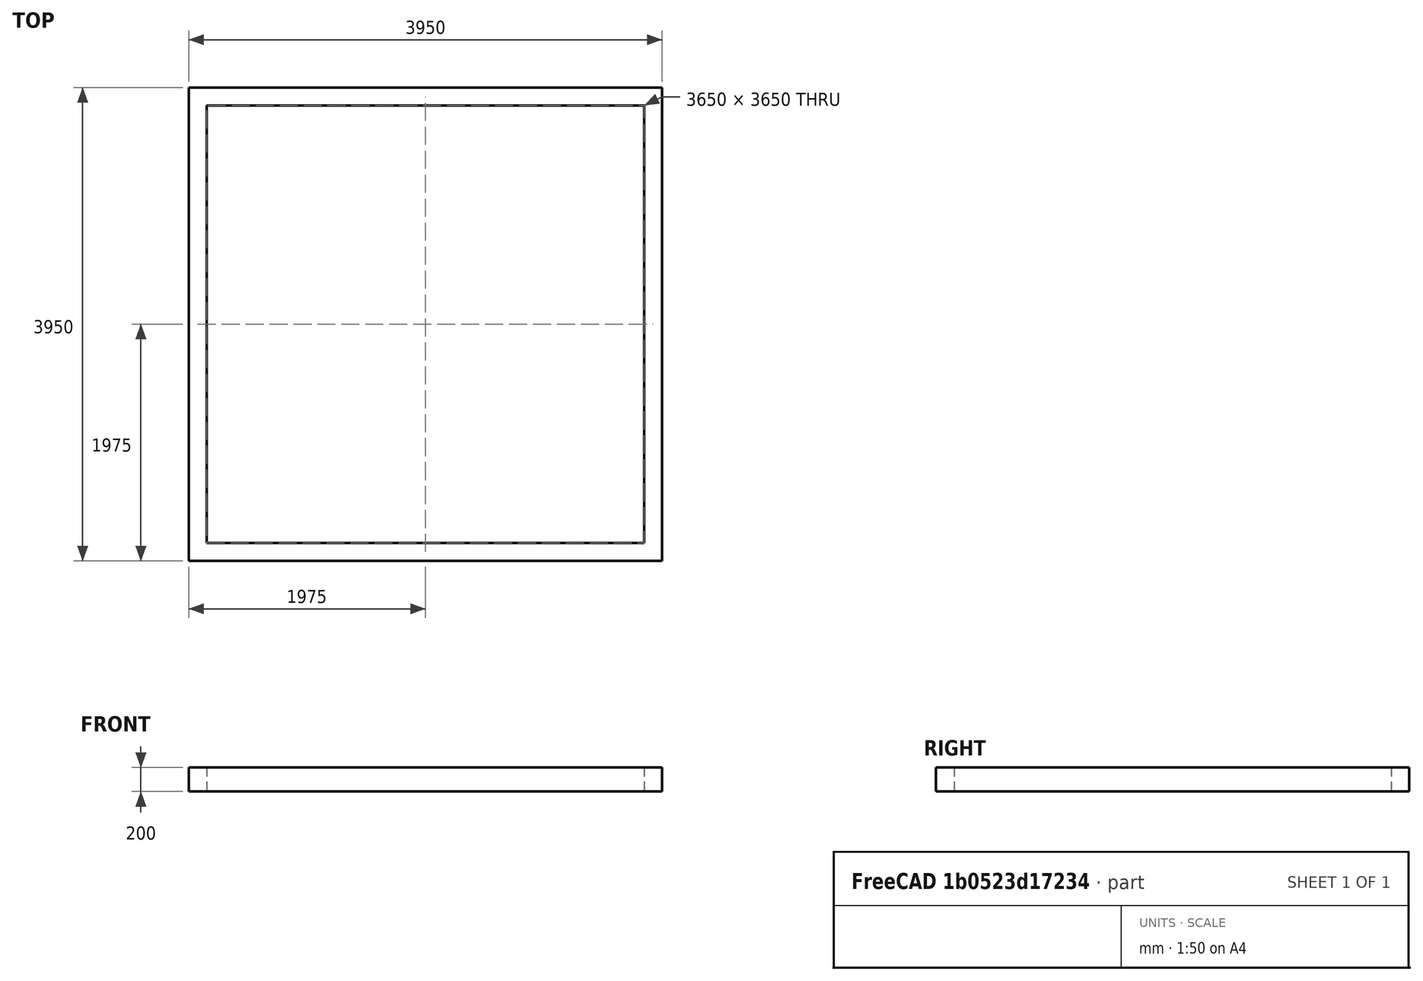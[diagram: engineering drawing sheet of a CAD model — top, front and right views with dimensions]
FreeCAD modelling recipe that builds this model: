
FCSTD DOCUMENT  (FreeCAD 0.20R29177 +426 (Git))
Label: ASM_Main
License: All rights reserved
LicenseURL: http://en.wikipedia.org/wiki/All_rights_reserved
objects: App::Link×4, App::DocumentObjectGroup×3, PartDesign::CoordinateSystem×1, App::FeaturePython×1, Part::FeaturePython×1, Sketcher::SketchObject×1, PartDesign::Pad×1, PartDesign::Body×1, App::Part×1
note: 6 computed .brp shape members not serialized (recipe doc carries the construction recipe); baked Part::Feature solids carry a one-line shape summary decoded from their .brp
EXTERNAL_REF file=ASM_Base.FCStd obj=LCS_Origin
EXTERNAL_REF file=ASM_Base.FCStd obj=Assembly
EXTERNAL_REF file=ASM_Platform.FCStd obj=ComputerPlatform_LCS_TopPivot
EXTERNAL_REF file=PlayStation5.FCStd obj=LCS_Origin
EXTERNAL_REF file=PlayStation5.FCStd obj=Assembly
EXTERNAL_REF file=ASM_TurnTable.FCStd obj=LCS_Origin
EXTERNAL_REF file=ASM_TurnTable.FCStd obj=Assembly
EXTERNAL_REF file=ASM_Platform.FCStd obj=Assembly
EXTERNAL_REF file=ASM_Platform.FCStd obj=LCS_Origin
EXTERNAL_REF file=Params.FCStd obj=Spreadsheet
EXTERNAL_REF file=../../../../../../AppData/Local/Temp/FreeCAD/Cache/FreeCAD_Doc_690303f0-95d3-45ba-b895-2698c964fae2_da39a3_1928 obj=LCS_Origin
EXTERNAL_REF file=../../../../../../AppData/Local/Temp/FreeCAD/Cache/FreeCAD_Doc_690303f0-95d3-45ba-b895-2698c964fae2_da39a3_1928 obj=Assembly
EXTERNAL_REF file=ASM_ExtensionArm.FCStd obj=Assembly

FEATURE [App::DocumentObjectGroup] Parts
FEATURE [PartDesign::CoordinateSystem] LCS_Origin
  AttacherType = Attacher::AttachEngine3D
  MapMode = 2
  Support = -> [X_Axis]
FEATURE [App::FeaturePython] Variables  # WARN: FeaturePython — macro-defined, semantics opaque (R4)
  Retraction = 0
  Rotation = 0
  Type = App::PropertyContainer
FEATURE [App::DocumentObjectGroup] Constraints
FEATURE [App::DocumentObjectGroup] Configurations
FEATURE [App::Link] ASM_Base
  AttachedBy = #LCS_Origin
  AttachedTo = Parent Assembly#LCS_Origin
  LinkedObject = -> <external ASM_Base.FCStd>#Assembly
  SolverId = Asm4EE
  expr: Placement = LCS_Origin.Placement * AttachmentOffset * ASM_Base#LCS_Origin.Placement ^ -1
FEATURE [App::Link] PlayStation5
  AttachedBy = #LCS_Origin
  AttachedTo = ASM_Platform#ComputerPlatform_LCS_TopPivot
  AttachmentOffset = pos=(0,-220,0) rot=(0,0,1;1.5708rad)
  LinkPlacement = pos=(0,-220,-100) rot=(0,0,1;1.5708rad)
  LinkedObject = -> <external PlayStation5.FCStd>#Assembly
  Placement = pos=(0,-220,-100) rot=(0,0,1;1.5708rad)
  SolverId = Asm4EE
  expr: Placement = ASM_Platform.Placement * ASM_Platform#ComputerPlatform_LCS_TopPivot.Placement * AttachmentOffset * PlayStation5#LCS_Origin.Placement ^ -1
FEATURE [App::Link] ASM_TurnTable
  AttachedBy = #LCS_Origin
  AttachedTo = ASM_Base#LCS_Origin
  AttachmentOffset = pos=(0,0,-20) rot=(0,0,1;0rad)
  LinkPlacement = pos=(0,0,-20) rot=(0,0,1;0rad)
  LinkedObject = -> <external ASM_TurnTable.FCStd>#Assembly
  Placement = pos=(0,0,-20) rot=(0,0,1;0rad)
  SolverId = Asm4EE
  expr: .AttachmentOffset.Rotation.Angle = <<Variables>>.Rotation
  expr: Placement = ASM_Base.Placement * ASM_Base#LCS_Origin.Placement * AttachmentOffset * ASM_TurnTable#LCS_Origin.Placement ^ -1
FEATURE [App::Link] ASM_Platform
  AttachedBy = #ComputerPlatform_LCS_TopPivot
  AttachedTo = ASM_TurnTable#LCS_Origin
  AttachmentOffset = pos=(0,0,-80) rot=(0,0,1;0rad)
  LinkPlacement = pos=(0,0,-102.656) rot=(0,0,1;0rad)
  LinkedObject = -> <external ASM_Platform.FCStd>#Assembly
  Placement = pos=(0,0,-102.656) rot=(0,0,1;0rad)
  SolverId = Asm4EE
  expr: Placement = ASM_TurnTable.Placement * ASM_TurnTable#LCS_Origin.Placement * AttachmentOffset * ASM_Platform#ComputerPlatform_LCS_TopPivot.Placement ^ -1
FEATURE [Part::FeaturePython] ASM_ExtensionArm_var  # link proxy (typed FeaturePython)
  AttachedBy = #LCS_Origin
  AttachedTo = ASM_Platform#LCS_Origin
  AttachmentOffset = pos=(23,0,0) rot=(0,0,1;0rad)
  LinkedObject = -> <external ../../../../../../AppData/Local/Temp/FreeCAD/Cache/FreeCAD_Doc_690303f0-95d3-45ba-b895-2698c964fae2_da39a3_1928>#Assembly
  Placement = pos=(23,0,-102.656) rot=(0,0,1;0rad)
  Retraction = 0
  SolverId = Asm4EE
  SourceObject = -> <external ASM_ExtensionArm.FCStd>#Assembly
  expr: .AttachmentOffset.Base.x = <<Params>>#<<Params>>.ExtensionArmCenterOffset
  expr: Placement = ASM_Platform.Placement * ASM_Platform#LCS_Origin.Placement * AttachmentOffset * varTmpDoc_2#LCS_Origin.Placement ^ -1
  expr: Retraction = <<Variables>>.Retraction
FEATURE [Sketcher::SketchObject] Sketch
  FullyConstrained = true
  MapMode = 5
  Support = -> [XY_Plane001]
  expr: Constraints[10] = <<Params>>#<<Params>>.RoomLength
  expr: Constraints[9] = <<Params>>#<<Params>>.RoomWidth
  sketch-geometry (11):
    g0: LineSegment StartX=-1825 StartY=-1825 StartZ=0 EndX=-1825 EndY=1825 EndZ=0
    g1: LineSegment StartX=-1825 StartY=1825 StartZ=0 EndX=1825 EndY=1825 EndZ=0
    g2: LineSegment StartX=1825 StartY=1825 StartZ=0 EndX=1825 EndY=-1825 EndZ=0
    g3: LineSegment StartX=1825 StartY=-1825 StartZ=0 EndX=-1825 EndY=-1825 EndZ=0
    g4: GeomPoint X=0 Y=0 Z=0
    g5: LineSegment StartX=1975 StartY=1975 StartZ=0 EndX=1975 EndY=-1975 EndZ=0
    g6: LineSegment StartX=1975 StartY=-1975 StartZ=0 EndX=-1975 EndY=-1975 EndZ=0
    g7: LineSegment StartX=-1975 StartY=-1975 StartZ=0 EndX=-1975 EndY=1975 EndZ=0
    g8: LineSegment StartX=-1975 StartY=1975 StartZ=0 EndX=1975 EndY=1975 EndZ=0
    g9: GeomPoint X=0 Y=0 Z=0
    g10: LineSegment StartX=-1825 StartY=1825 StartZ=0 EndX=-1975 EndY=1975 EndZ=0
  constraints (26):
    c: Coincident(g0,g1)
    c: Coincident(g1,g2)
    c: Coincident(g2,g3)
    c: Coincident(g3,g0)
    c: Horizontal(g1)
    c: Horizontal(g3)
    c: Vertical(g0)
    c: Vertical(g2)
    c: Symmetric(g1,g0,g4)
    c: DistanceY(g2,g2) = 3650
    c: DistanceX(g3,g3) = 3650
    c: Coincident(g5,g6)
    c: Coincident(g6,g7)
    c: Coincident(g7,g8)
    c: Coincident(g8,g5)
    c: Horizontal(g6)
    c: Horizontal(g8)
    c: Vertical(g5)
    c: Vertical(g7)
    c: Symmetric(g6,g5,g9)
    c: Coincident(g9,g4)
    c: Coincident(g10,g0)
    c: Coincident(g10,g7)
    c: Angle(g10,g8) = 0.785398
    c: DistanceY(g0,g7) = 150
    c: Coincident(g4,g-1)
FEATURE [PartDesign::Pad] Pad
  Direction = (0,0,1)
  Length = 200
  Length2 = 10
  Profile = -> Sketch
  ReferenceAxis = -> Sketch [N_Axis]
  Reversed = true
  Type = 0
  expr: Length = 200
FEATURE [PartDesign::Body] Body  label="Room"
  Group = -> [Sketch,Pad]
  Origin = -> Origin001
  Tip = -> Pad
FEATURE [App::Part] Assembly
  AssemblyType = Part::Link
  Group = -> [LCS_Origin,Variables,Constraints,Configurations,ASM_Base,PlayStation5,ASM_TurnTable,ASM_Platform,ASM_ExtensionArm_var,Body]
  Origin = -> Origin
  Type = Assembly

RESOLVED EXTERNAL PARTS (link-assembly join: the EXTERNAL_REF files above that resolve inside this repo's crawl, each included once):
---- part ASM_Base.FCStd = doc fcstd_a2ac483629b0 ----
FCSTD DOCUMENT  (FreeCAD 0.20R29177 +426 (Git))
Label: ASM_Base
License: All rights reserved
LicenseURL: http://en.wikipedia.org/wiki/All_rights_reserved
objects: App::Link×6, App::DocumentObjectGroup×3, PartDesign::CoordinateSystem×1, App::FeaturePython×1, App::Part×1
note: 1 computed .brp shape members not serialized (recipe doc carries the construction recipe); baked Part::Feature solids carry a one-line shape summary decoded from their .brp
EXTERNAL_REF file=CeilingPlate.FCStd obj=LCS_Origin
EXTERNAL_REF file=PipeFloorFlange.FCStd obj=LCS_1
EXTERNAL_REF file=PipeFloorFlange.FCStd obj=Body
EXTERNAL_REF file=PipeNipple.FCStd obj=LCS_root
EXTERNAL_REF file=PipeNipple.FCStd obj=Body
EXTERNAL_REF file=PipeNipple.FCStd obj=LCS_end
EXTERNAL_REF file=SlipRing.FCStd obj=LCS_Origin
EXTERNAL_REF file=SlipRing.FCStd obj=Assembly
EXTERNAL_REF file=CeilingPlate.FCStd obj=Assembly
EXTERNAL_REF file=CeilingPlate.FCStd obj=Pad
EXTERNAL_REF file=CeilingPlate.FCStd obj=Sketch001
EXTERNAL_REF file=StrutChannelHalf.FCStd obj=LCS_Face
EXTERNAL_REF file=StrutChannelHalf.FCStd obj=Assembly

FEATURE [App::DocumentObjectGroup] Parts
FEATURE [PartDesign::CoordinateSystem] LCS_Origin
  AttacherType = Attacher::AttachEngine3D
  MapMode = 2
  Support = -> [X_Axis]
FEATURE [App::FeaturePython] Variables  # WARN: FeaturePython — macro-defined, semantics opaque (R4)
  Type = App::PropertyContainer
FEATURE [App::DocumentObjectGroup] Constraints
FEATURE [App::DocumentObjectGroup] Configurations
FEATURE [App::Link] PipeFlange
  AssemblyType = Part::Link
  AttachedBy = #LCS_1
  AttachedTo = CeilingPlate#LCS_Origin
  AttachmentOffset = pos=(0,0,0) rot=(1,0,0;3.14159rad)
  LinkPlacement = pos=(0,0,0) rot=(1,0,0;3.14159rad)
  LinkedObject = -> <external PipeFloorFlange.FCStd>#Body
  Placement = pos=(0,0,0) rot=(1,0,0;3.14159rad)
  SolverId = Asm4EE
  expr: Placement = CeilingPlate.Placement * CeilingPlate#LCS_Origin.Placement * AttachmentOffset * PipeFloorFlange#LCS_1.Placement ^ -1
FEATURE [App::Link] PipeNipple
  AssemblyType = Part::Link
  AttachedBy = #LCS_root
  AttachedTo = PipeFlange#LCS_1
  LinkPlacement = pos=(0,0,0) rot=(1,0,0;3.14159rad)
  LinkedObject = -> <external PipeNipple.FCStd>#Body
  Placement = pos=(0,0,0) rot=(1,0,0;3.14159rad)
  SolverId = Asm4EE
  expr: Placement = PipeFlange.Placement * PipeFloorFlange#LCS_1.Placement * AttachmentOffset * PipeNipple#LCS_root.Placement ^ -1
FEATURE [App::Link] SlipRing
  AttachedBy = #LCS_Origin
  AttachedTo = PipeNipple#LCS_end
  AttachmentOffset = pos=(0,0,0) rot=(1,0,0;3.14159rad)
  LinkPlacement = pos=(0,-1.09e-14,-88.9) rot=(0,0,1;0rad)
  LinkedObject = -> <external SlipRing.FCStd>#Assembly
  Placement = pos=(0,-1.09e-14,-88.9) rot=(0,0,1;0rad)
  SolverId = Asm4EE
  expr: Placement = PipeNipple.Placement * PipeNipple#LCS_end.Placement * AttachmentOffset * SlipRing#LCS_Origin.Placement ^ -1
FEATURE [App::Link] CeilingPlate
  AttachedBy = #LCS_Origin
  AttachedTo = Parent Assembly#LCS_Origin
  LinkedObject = -> <external CeilingPlate.FCStd>#Assembly
  SolverId = Asm4EE
  expr: Placement = LCS_Origin.Placement * AttachmentOffset * CeilingPlate#LCS_Origin.Placement ^ -1
FEATURE [App::Link] StrutChannelHalf
  AttachedBy = #LCS_Face
  AttachedTo = Parent Assembly#LCS_Origin
  AttachmentOffset = pos=(135.057,0,18.5) rot=(1,0,0;4.71239rad)
  LinkPlacement = pos=(135.057,4.6e-15,39.14) rot=(1,0,0;4.71239rad)
  LinkedObject = -> <external StrutChannelHalf.FCStd>#Assembly
  Placement = pos=(135.057,4.6e-15,39.14) rot=(1,0,0;4.71239rad)
  SolverId = Asm4EE
  expr: .AttachmentOffset.Base.x = <<CeilingPlate>>#<<Sketch001>>.Constraints.CeilingRailSpacing / 2
  expr: .AttachmentOffset.Base.z = <<CeilingPlate>>#<<Pad>>.Length
  expr: Placement = LCS_Origin.Placement * AttachmentOffset * StrutChannelHalf#LCS_Face.Placement ^ -1
FEATURE [App::Link] StrutChannelHalf001
  AttachedBy = #LCS_Face
  AttachedTo = Parent Assembly#LCS_Origin
  AttachmentOffset = pos=(-135.057,0,18.5) rot=(1,0,0;4.71239rad)
  LinkPlacement = pos=(-135.057,4.6e-15,39.14) rot=(1,0,0;4.71239rad)
  LinkedObject = -> <external StrutChannelHalf.FCStd>#Assembly
  Placement = pos=(-135.057,4.6e-15,39.14) rot=(1,0,0;4.71239rad)
  SolverId = Asm4EE
  expr: .AttachmentOffset.Base.x = <<CeilingPlate>>#<<Sketch001>>.Constraints.CeilingRailSpacing / -2
  expr: .AttachmentOffset.Base.z = <<CeilingPlate>>#<<Pad>>.Length
  expr: Placement = LCS_Origin.Placement * AttachmentOffset * StrutChannelHalf#LCS_Face.Placement ^ -1
FEATURE [App::Part] Assembly
  AssemblyType = Part::Link
  Group = -> [LCS_Origin,Variables,Constraints,Configurations,PipeFlange,PipeNipple,SlipRing,CeilingPlate,StrutChannelHalf,StrutChannelHalf001]
  LabelDocUser = ASM_Base
  LabelPartUser = Assembly
  Origin = -> Origin
  Type = Assembly
---- part ASM_ExtensionArm.FCStd = doc fcstd_39be14f38531 ----
FCSTD DOCUMENT  (FreeCAD 0.20R29177 +426 (Git))
Label: ASM_ExtensionArm
License: All rights reserved
LicenseURL: http://en.wikipedia.org/wiki/All_rights_reserved
objects: App::Link×7, App::DocumentObjectGroup×4, PartDesign::CoordinateSystem×3, App::FeaturePython×1, Part::FeaturePython×1, App::Part×1
note: 4 computed .brp shape members not serialized (recipe doc carries the construction recipe); baked Part::Feature solids carry a one-line shape summary decoded from their .brp
EXTERNAL_REF file=ASM_GantrySkate.FCStd obj=LCS_Origin
EXTERNAL_REF file=Params.FCStd obj=Spreadsheet
EXTERNAL_REF file=ASM_GantrySkate.FCStd obj=Assembly
EXTERNAL_REF file=../../../../../../AppData/Local/Temp/FreeCAD/Cache/FreeCAD_Doc_665ddbc1-c403-4c85-9c79-733a05948db3_da39a3_5468 obj=Assembly
EXTERNAL_REF file=AlExtrusion2040.FCStd obj=Assembly
EXTERNAL_REF file=ASM_ExtensionDriver.FCStd obj=LCS_Origin
EXTERNAL_REF file=ASM_ExtensionDriver.FCStd obj=Assembly
EXTERNAL_REF file=EndStopRear.FCStd obj=LCS_Origin
EXTERNAL_REF file=EndStopRear.FCStd obj=Assembly
EXTERNAL_REF file=BeltRetainerRear.FCStd obj=LCS_Origin
EXTERNAL_REF file=BeltRetainerRear.FCStd obj=Assembly
EXTERNAL_REF file=ASM_ExtensionHead.FCStd obj=LCS_Origin
EXTERNAL_REF file=ASM_ExtensionHead.FCStd obj=Assembly

FEATURE [App::DocumentObjectGroup] Parts
FEATURE [PartDesign::CoordinateSystem] LCS_Origin
  AttacherType = Attacher::AttachEngine3D
  MapMode = 2
  Support = -> [X_Axis]
FEATURE [App::FeaturePython] Variables  # WARN: FeaturePython — macro-defined, semantics opaque (R4)
  Retraction = 300
  Type = App::PropertyContainer
FEATURE [App::DocumentObjectGroup] Constraints
FEATURE [App::DocumentObjectGroup] Configurations
FEATURE [App::Link] ASM_GantrySkate  label="ASM_GantrySkate001"
  AttachedBy = #LCS_Origin
  AttachedTo = Parent Assembly#LCS_Origin
  AttachmentOffset = pos=(0,-150,0) rot=(0,1,0;3.14159rad)
  LinkPlacement = pos=(0,-150,0) rot=(0,1,0;3.14159rad)
  LinkedObject = -> <external ASM_GantrySkate.FCStd>#Assembly
  Placement = pos=(0,-150,0) rot=(0,1,0;3.14159rad)
  SolverId = Asm4EE
  expr: .AttachmentOffset.Base.y = <<Params>>#<<Params>>.RearSkateOffset * -1
  expr: Placement = LCS_Origin.Placement * AttachmentOffset * ASM_GantrySkate#LCS_Origin.Placement ^ -1
FEATURE [App::Link] ASM_GantrySkate001  label="ASM_GantrySkate002"
  AttachedBy = #LCS_Origin
  AttachedTo = Parent Assembly#LCS_Origin
  AttachmentOffset = pos=(0,350,0) rot=(0,1,0;3.14159rad)
  LinkPlacement = pos=(0,350,0) rot=(0,1,0;3.14159rad)
  LinkedObject = -> <external ASM_GantrySkate.FCStd>#Assembly
  Placement = pos=(0,350,0) rot=(0,1,0;3.14159rad)
  SolverId = Asm4EE
  expr: .AttachmentOffset.Base.y = <<Params>>#<<Params>>.FrontSkateOffset
  expr: Placement = LCS_Origin.Placement * AttachmentOffset * ASM_GantrySkate#LCS_Origin.Placement ^ -1
FEATURE [Part::FeaturePython] AlExtrusion2040_var  # link proxy (typed FeaturePython)
  AttachedBy = #LCS_Origin
  AttachedTo = Parent Assembly#LCS_EndStop
  AttachmentOffset = pos=(0,0,0) rot=(0.57735,-0.57735,-0.57735;4.18879rad)
  Length = 2000
  LinkedObject = -> <external ../../../../../../AppData/Local/Temp/FreeCAD/Cache/FreeCAD_Doc_665ddbc1-c403-4c85-9c79-733a05948db3_da39a3_5468>#Assembly
  Placement = pos=(2.9e-15,-482,-23.5) rot=(-0.57735,-0.57735,-0.57735;2.0944rad)
  SolverId = Asm4EE
  SourceObject = -> <external AlExtrusion2040.FCStd>#Assembly
  expr: Placement = LCS_EndStop.Placement * AttachmentOffset * varTmpDoc_3#LCS_Origin.Placement ^ -1
FEATURE [App::Link] ASM_ExtensionDriver
  AttachedBy = #LCS_Origin
  AttachedTo = Parent Assembly#LCS_Origin
  AttachmentOffset = pos=(-36,100,0) rot=(0.707107,0.707107,0;3.14159rad)
  LinkPlacement = pos=(-36,100,0) rot=(0.707107,0.707107,0;3.14159rad)
  LinkedObject = -> <external ASM_ExtensionDriver.FCStd>#Assembly
  Placement = pos=(-36,100,0) rot=(0.707107,0.707107,0;3.14159rad)
  SolverId = Asm4EE
  expr: Placement = LCS_Origin.Placement * AttachmentOffset * ASM_ExtensionDriver#LCS_Origin.Placement ^ -1
FEATURE [App::DocumentObjectGroup] Fasteners
FEATURE [App::Link] EndStopRear
  AttachedBy = #LCS_Origin
  AttachedTo = Parent Assembly#LCS_EndStop
  AttachmentOffset = pos=(0,0,0) rot=(1,0,0;1.5708rad)
  LinkPlacement = pos=(2.9e-15,-482,-23.5) rot=(0,0.707107,-0.707107;3.14159rad)
  LinkedObject = -> <external EndStopRear.FCStd>#Assembly
  Placement = pos=(2.9e-15,-482,-23.5) rot=(0,0.707107,-0.707107;3.14159rad)
  SolverId = Asm4EE
  expr: Placement = LCS_EndStop.Placement * AttachmentOffset * EndStopRear#LCS_Origin.Placement ^ -1
FEATURE [PartDesign::CoordinateSystem] ASM_GantrySkate_LCS_Origin
  AttachedBy = Origin
  AttacherType = Attacher::AttachEngine3D
  Placement = pos=(0,-150,0) rot=(0,1,0;3.14159rad)
  SolverId = Asm4EE
  expr: Placement = ASM_GantrySkate.Placement * ASM_GantrySkate#LCS_Origin.Placement
FEATURE [PartDesign::CoordinateSystem] LCS_EndStop
  AttacherType = Attacher::AttachEngine3D
  AttachmentOffset = pos=(0,-332,23.5) rot=(0,0,1;0rad)
  MapMode = 2
  Placement = pos=(2.9e-15,-482,-23.5) rot=(0,1,0;3.14159rad)
  Support = -> [ASM_GantrySkate_LCS_Origin]
  expr: .AttachmentOffset.Base.y = -32 - <<Variables>>.Retraction
FEATURE [App::Link] BeltRetainerRear
  AttachedBy = #LCS_Origin
  AttachedTo = Parent Assembly#LCS_EndStop
  AttachmentOffset = pos=(10,30,10) rot=(0.57735,0.57735,0.57735;2.0944rad)
  LinkPlacement = pos=(-10,-452,-33.5) rot=(0.57735,0.57735,-0.57735;4.18879rad)
  LinkedObject = -> <external BeltRetainerRear.FCStd>#Assembly
  Placement = pos=(-10,-452,-33.5) rot=(0.57735,0.57735,-0.57735;4.18879rad)
  SolverId = Asm4EE
  expr: Placement = LCS_EndStop.Placement * AttachmentOffset * BeltRetainerRear#LCS_Origin.Placement ^ -1
FEATURE [App::Link] BeltRetainerRear001  label="BeltRetainerTip"
  AttachedBy = #LCS_Origin
  AttachedTo = Parent Assembly#LCS_EndStop
  AttachmentOffset = pos=(10,1977,10) rot=(0.57735,-0.57735,0.57735;4.18879rad)
  LinkPlacement = pos=(-10,1495,-33.5) rot=(0.57735,-0.57735,-0.57735;2.0944rad)
  LinkedObject = -> <external BeltRetainerRear.FCStd>#Assembly
  Placement = pos=(-10,1495,-33.5) rot=(0.57735,-0.57735,-0.57735;2.0944rad)
  SolverId = Asm4EE
  expr: Placement = LCS_EndStop.Placement * AttachmentOffset * BeltRetainerRear#LCS_Origin.Placement ^ -1
FEATURE [App::Link] ASM_ExtensionHead
  AttachedBy = #LCS_Origin
  AttachedTo = Parent Assembly#LCS_EndStop
  AttachmentOffset = pos=(0,2000,0) rot=(0,1,0;3.14159rad)
  LinkPlacement = pos=(2.9e-15,1518,-23.5) rot=(0,0,1;0rad)
  LinkedObject = -> <external ASM_ExtensionHead.FCStd>#Assembly
  Placement = pos=(2.9e-15,1518,-23.5) rot=(0,0,1;0rad)
  SolverId = Asm4EE
  expr: .AttachmentOffset.Base.y = <<AlExtrusion2040_var>>.Length
  expr: Placement = LCS_EndStop.Placement * AttachmentOffset * ASM_ExtensionHead#LCS_Origin.Placement ^ -1
FEATURE [App::Part] Assembly
  AssemblyType = Part::Link
  Group = -> [LCS_Origin,Variables,Constraints,Configurations,ASM_GantrySkate,ASM_GantrySkate001,AlExtrusion2040_var,ASM_ExtensionDriver,Fasteners,EndStopRear,LCS_EndStop,ASM_GantrySkate_LCS_Origin,BeltRetainerRear,BeltRetainerRear001,ASM_ExtensionHead]
  Origin = -> Origin
  Type = Assembly
---- part ASM_Platform.FCStd = doc fcstd_33a8892f44dc ----
FCSTD DOCUMENT  (FreeCAD 0.20R29177 +426 (Git))
Label: ASM_Platform
License: All rights reserved
LicenseURL: http://en.wikipedia.org/wiki/All_rights_reserved
objects: App::DocumentObjectGroup×3, App::Link×3, PartDesign::CoordinateSystem×2, App::FeaturePython×1, App::Part×1
note: 2 computed .brp shape members not serialized (recipe doc carries the construction recipe); baked Part::Feature solids carry a one-line shape summary decoded from their .brp
EXTERNAL_REF file=ComputerPlatform.FCStd obj=LCS_Origin
EXTERNAL_REF file=ComputerPlatform.FCStd obj=Assembly
EXTERNAL_REF file=ComputerPlatform.FCStd obj=LCS_TopPivot
EXTERNAL_REF file=ComputerPlatformRib.FCStd obj=LCS_Origin
EXTERNAL_REF file=ComputerPlatformRib.FCStd obj=Assembly

FEATURE [App::DocumentObjectGroup] Parts
FEATURE [PartDesign::CoordinateSystem] LCS_Origin
  AttacherType = Attacher::AttachEngine3D
  MapMode = 2
  Support = -> [X_Axis]
FEATURE [App::FeaturePython] Variables  # WARN: FeaturePython — macro-defined, semantics opaque (R4)
  RibOffset = 70
  Type = App::PropertyContainer
FEATURE [App::DocumentObjectGroup] Constraints
FEATURE [App::DocumentObjectGroup] Configurations
FEATURE [App::Link] ComputerPlatform
  AttachedBy = #LCS_Origin
  AttachedTo = Parent Assembly#LCS_Origin
  LinkedObject = -> <external ComputerPlatform.FCStd>#Assembly
  SolverId = Asm4EE
  expr: Placement = LCS_Origin.Placement * AttachmentOffset * ComputerPlatform#LCS_Origin.Placement ^ -1
FEATURE [PartDesign::CoordinateSystem] ComputerPlatform_LCS_TopPivot
  AttachedBy = Origin
  AttacherType = Attacher::AttachEngine3D
  Placement = pos=(0,0,2.656) rot=(0,0,1;0rad)
  SolverId = Asm4EE
  expr: Placement = ComputerPlatform.Placement * ComputerPlatform#LCS_TopPivot.Placement
FEATURE [App::Link] ComputerPlatformRib
  AttachedBy = #LCS_Origin
  AttachedTo = ComputerPlatform#LCS_Origin
  AttachmentOffset = pos=(70,0,0) rot=(0,0,1;0rad)
  LinkPlacement = pos=(70,0,0) rot=(0,0,1;0rad)
  LinkedObject = -> <external ComputerPlatformRib.FCStd>#Assembly
  Placement = pos=(70,0,0) rot=(0,0,1;0rad)
  SolverId = Asm4EE
  expr: .AttachmentOffset.Base.x = <<Variables>>.RibOffset
  expr: Placement = ComputerPlatform.Placement * ComputerPlatform#LCS_Origin.Placement * AttachmentOffset * ComputerPlatformRib#LCS_Origin.Placement ^ -1
FEATURE [App::Link] ComputerPlatformRib001
  AttachedBy = #LCS_Origin
  AttachedTo = ComputerPlatform#LCS_Origin
  AttachmentOffset = pos=(-70,0,0) rot=(0,0,1;0rad)
  LinkPlacement = pos=(-70,0,0) rot=(0,0,1;0rad)
  LinkedObject = -> <external ComputerPlatformRib.FCStd>#Assembly
  Placement = pos=(-70,0,0) rot=(0,0,1;0rad)
  SolverId = Asm4EE
  expr: .AttachmentOffset.Base.x = <<Variables>>.RibOffset * -1
  expr: Placement = ComputerPlatform.Placement * ComputerPlatform#LCS_Origin.Placement * AttachmentOffset * ComputerPlatformRib#LCS_Origin.Placement ^ -1
FEATURE [App::Part] Assembly
  AssemblyType = Part::Link
  Group = -> [LCS_Origin,Variables,Constraints,Configurations,ComputerPlatform,ComputerPlatform_LCS_TopPivot,ComputerPlatformRib,ComputerPlatformRib001]
  Origin = -> Origin
  Type = Assembly
---- part ASM_TurnTable.FCStd = doc fcstd_badc906776cf ----
FCSTD DOCUMENT  (FreeCAD 0.20R29177 +426 (Git))
Label: ASM_TurnTable
License: All rights reserved
LicenseURL: http://en.wikipedia.org/wiki/All_rights_reserved
objects: App::Link×9, App::DocumentObjectGroup×3, PartDesign::CoordinateSystem×1, App::FeaturePython×1, App::Part×1
note: 1 computed .brp shape members not serialized (recipe doc carries the construction recipe); baked Part::Feature solids carry a one-line shape summary decoded from their .brp
EXTERNAL_REF file=DrivePlatform.FCStd obj=LCS_Origin
EXTERNAL_REF file=Params.FCStd obj=Spreadsheet
EXTERNAL_REF file=PillowBlock.FCStd obj=LCS_Origin
EXTERNAL_REF file=PillowBlock.FCStd obj=Assembly
EXTERNAL_REF file=DrivePlatform.FCStd obj=Assembly
EXTERNAL_REF file=ASM_TableRoller.FCStd obj=LCS_Origin
EXTERNAL_REF file=DrivePlatform.FCStd obj=LCS_RollerDriveSupport1
EXTERNAL_REF file=ASM_TableRoller.FCStd obj=Assembly
EXTERNAL_REF file=DrivePlatform.FCStd obj=LCS_RollerDriveSupport2
EXTERNAL_REF file=DrivePlatform.FCStd obj=LCS_RollerSide1
EXTERNAL_REF file=DrivePlatform.FCStd obj=LCS_RollerSide2
EXTERNAL_REF file=ASM_RotationDriver.FCStd obj=LCS_Origin
EXTERNAL_REF file=RotationDriverMountingSpacer.FCStd obj=Pad
EXTERNAL_REF file=ASM_RotationDriver.FCStd obj=Assembly
EXTERNAL_REF file=DrivePlatformRib.FCStd obj=LCS_Origin
EXTERNAL_REF file=DrivePlatformRib.FCStd obj=Assembly

FEATURE [App::DocumentObjectGroup] Parts
FEATURE [PartDesign::CoordinateSystem] LCS_Origin
  AttacherType = Attacher::AttachEngine3D
  MapMode = 2
  Support = -> [X_Axis]
FEATURE [App::FeaturePython] Variables  # WARN: FeaturePython — macro-defined, semantics opaque (R4)
  RibOffset = 70
  Type = App::PropertyContainer
FEATURE [App::DocumentObjectGroup] Constraints
FEATURE [App::DocumentObjectGroup] Configurations
FEATURE [App::Link] PillowBlock
  AttachedBy = #LCS_Origin
  AttachedTo = DrivePlatform#LCS_Origin
  AttachmentOffset = pos=(0,0,2.656) rot=(0,0,1;0rad)
  LinkPlacement = pos=(9e-16,0,-2.656) rot=(0,-1,0;3.14159rad)
  LinkedObject = -> <external PillowBlock.FCStd>#Assembly
  Placement = pos=(9e-16,0,-2.656) rot=(0,-1,0;3.14159rad)
  SolverId = Asm4EE
  expr: .AttachmentOffset.Base.z = <<Params>>#<<Params>>.SheetMetalThickness
  expr: Placement = DrivePlatform.Placement * DrivePlatform#LCS_Origin.Placement * AttachmentOffset * PillowBlock#LCS_Origin.Placement ^ -1
FEATURE [App::Link] DrivePlatform
  AttachedBy = #LCS_Origin
  AttachedTo = Parent Assembly#LCS_Origin
  AttachmentOffset = pos=(0,0,0) rot=(0,-1,0;3.14159rad)
  LinkPlacement = pos=(0,0,0) rot=(0,-1,0;3.14159rad)
  LinkedObject = -> <external DrivePlatform.FCStd>#Assembly
  Placement = pos=(0,0,0) rot=(0,-1,0;3.14159rad)
  SolverId = Asm4EE
  expr: Placement = LCS_Origin.Placement * AttachmentOffset * DrivePlatform#LCS_Origin.Placement ^ -1
FEATURE [App::Link] ASM_TableRoller
  AttachedBy = #LCS_Origin
  AttachedTo = DrivePlatform#LCS_RollerDriveSupport1
  AttachmentOffset = pos=(0,0,0) rot=(1,0,0;3.14159rad)
  LinkPlacement = pos=(50.8911,211.977,1.64e-14) rot=(0,0,1;2.90597rad)
  LinkedObject = -> <external ASM_TableRoller.FCStd>#Assembly
  Placement = pos=(50.8911,211.977,1.64e-14) rot=(0,0,1;2.90597rad)
  SolverId = Asm4EE
  expr: Placement = DrivePlatform.Placement * DrivePlatform#LCS_RollerDriveSupport1.Placement * AttachmentOffset * ASM_TableRoller#LCS_Origin.Placement ^ -1
FEATURE [App::Link] ASM_TableRoller001
  AttachedBy = #LCS_Origin
  AttachedTo = DrivePlatform#LCS_RollerDriveSupport2
  AttachmentOffset = pos=(0,0,0) rot=(1,0,0;3.14159rad)
  LinkPlacement = pos=(-50.8911,211.977,-1.64e-14) rot=(0,0,1;3.37721rad)
  LinkedObject = -> <external ASM_TableRoller.FCStd>#Assembly
  Placement = pos=(-50.8911,211.977,-1.64e-14) rot=(0,0,1;3.37721rad)
  SolverId = Asm4EE
  expr: Placement = DrivePlatform.Placement * DrivePlatform#LCS_RollerDriveSupport2.Placement * AttachmentOffset * ASM_TableRoller#LCS_Origin.Placement ^ -1
FEATURE [App::Link] ASM_TableRoller002
  AttachedBy = #LCS_Origin
  AttachedTo = DrivePlatform#LCS_RollerSide1
  AttachmentOffset = pos=(0,0,0) rot=(0.707107,0.707107,0;3.14159rad)
  LinkPlacement = pos=(154.11,-56.0913,4.96e-14) rot=(0,0,1;1.22173rad)
  LinkedObject = -> <external ASM_TableRoller.FCStd>#Assembly
  Placement = pos=(154.11,-56.0913,4.96e-14) rot=(0,0,1;1.22173rad)
  SolverId = Asm4EE
  expr: Placement = DrivePlatform.Placement * DrivePlatform#LCS_RollerSide1.Placement * AttachmentOffset * ASM_TableRoller#LCS_Origin.Placement ^ -1
FEATURE [App::Link] ASM_TableRoller003
  AttachedBy = #LCS_Origin
  AttachedTo = DrivePlatform#LCS_RollerSide2
  AttachmentOffset = pos=(0,0,0) rot=(0.707107,-0.707107,0;3.14159rad)
  LinkPlacement = pos=(-154.11,-56.0913,-4.96e-14) rot=(0,0,1;5.06145rad)
  LinkedObject = -> <external ASM_TableRoller.FCStd>#Assembly
  Placement = pos=(-154.11,-56.0913,-4.96e-14) rot=(0,0,1;5.06145rad)
  SolverId = Asm4EE
  expr: Placement = DrivePlatform.Placement * DrivePlatform#LCS_RollerSide2.Placement * AttachmentOffset * ASM_TableRoller#LCS_Origin.Placement ^ -1
FEATURE [App::Link] ASM_RotationDriver
  AttachedBy = #LCS_Origin
  AttachedTo = DrivePlatform#LCS_Origin
  AttachmentOffset = pos=(0,260.5,-9) rot=(1,0,0;4.71239rad)
  LinkPlacement = pos=(-2.9e-15,260.5,9) rot=(0,0.707107,0.707107;3.14159rad)
  LinkedObject = -> <external ASM_RotationDriver.FCStd>#Assembly
  Placement = pos=(-2.9e-15,260.5,9) rot=(0,0.707107,0.707107;3.14159rad)
  SolverId = Asm4EE
  expr: .AttachmentOffset.Base.y = <<Params>>#<<Params>>.CeilingPlateDiameter / 2 + <<Params>>#<<Params>>.RotationDriveOffset
  expr: .AttachmentOffset.Base.z = <<RotationDriverMountingSpacer>>#<<Pad>>.Length * -1
  expr: Placement = DrivePlatform.Placement * DrivePlatform#LCS_Origin.Placement * AttachmentOffset * ASM_RotationDriver#LCS_Origin.Placement ^ -1
FEATURE [App::Link] DrivePlatformRib
  AttachedBy = #LCS_Origin
  AttachedTo = DrivePlatform#LCS_Origin
  AttachmentOffset = pos=(70,0,2.656) rot=(-0.707107,-0.707107,0;3.14159rad)
  LinkPlacement = pos=(-70,0,-2.656) rot=(0,0,-1;4.71239rad)
  LinkedObject = -> <external DrivePlatformRib.FCStd>#Assembly
  Placement = pos=(-70,0,-2.656) rot=(0,0,-1;4.71239rad)
  SolverId = Asm4EE
  expr: .AttachmentOffset.Base.x = <<Variables>>.RibOffset
  expr: .AttachmentOffset.Base.z = <<Params>>#<<Params>>.SheetMetalThickness
  expr: Placement = DrivePlatform.Placement * DrivePlatform#LCS_Origin.Placement * AttachmentOffset * DrivePlatformRib#LCS_Origin.Placement ^ -1
FEATURE [App::Link] DrivePlatformRib001
  AttachedBy = #LCS_Origin
  AttachedTo = DrivePlatform#LCS_Origin
  AttachmentOffset = pos=(-70,0,2.656) rot=(-0.707107,-0.707107,0;3.14159rad)
  LinkPlacement = pos=(70,0,-2.656) rot=(0,0,-1;4.71239rad)
  LinkedObject = -> <external DrivePlatformRib.FCStd>#Assembly
  Placement = pos=(70,0,-2.656) rot=(0,0,-1;4.71239rad)
  SolverId = Asm4EE
  expr: .AttachmentOffset.Base.x = <<Variables>>.RibOffset * -1
  expr: .AttachmentOffset.Base.z = <<Params>>#<<Params>>.SheetMetalThickness
  expr: Placement = DrivePlatform.Placement * DrivePlatform#LCS_Origin.Placement * AttachmentOffset * DrivePlatformRib#LCS_Origin.Placement ^ -1
FEATURE [App::Part] Assembly
  AssemblyType = Part::Link
  Group = -> [LCS_Origin,Variables,Constraints,Configurations,PillowBlock,DrivePlatform,ASM_TableRoller,ASM_TableRoller001,ASM_TableRoller002,ASM_TableRoller003,ASM_RotationDriver,DrivePlatformRib,DrivePlatformRib001]
  Origin = -> Origin
  Type = Assembly
---- part Params.FCStd = doc fcstd_b8f81ed59c9d ----
FCSTD DOCUMENT  (FreeCAD 0.20R29177 +426 (Git))
Label: Params
License: All rights reserved
LicenseURL: http://en.wikipedia.org/wiki/All_rights_reserved
objects: Spreadsheet::Sheet×1

FEATURE [Spreadsheet::Sheet] Spreadsheet  label="Params"
  cells = A1=DriveWheelWidth; B1(DriveWheelWidth)=10; D1=PlywoodThickness; E1(PlywoodThickness)=18.5; A2=DriveWheelMajorDiameter; B2(DriveWheelMajorDiameter)=52; D2=ExtensionArmCenterOffset; E2(ExtensionArmCenterOffset)=23; A3=DriveWheelCrown; B3(DriveWheelCrown)=2; D3=SheetMetalThickness; E3(SheetMetalThickness)=2.656; A4=DriveWheelTireThickness; B4(DriveWheelTireThickness)=3; D4=CeilingPlateDiameter; E4(CeilingPlateDiameter)=463; A6=DriveUnitAngle; B6(DriveUnitAngle)=30; D6=TableRollerMountHoleSpacing; E6(TableRollerMountHoleSpacing)=24; A7=DriveRadius; B7(DriveRadius)=280; D7=TableRollerMountHoleOffset; E7(TableRollerMountHoleOffset)=12; A8=DriveAdjMiddleOffset; B8(DriveAdjMiddleOffset)=90; D8=TableRollerDriveSupportRadius; E8(TableRollerDriveSupportRadius)=218; A9=RotationDriveOffset; B9(RotationDriveOffset)=29; D9=TableRollerSideRadius; E9(TableRollerSideRadius)=164; A10=FrontSkateOffset; B10(FrontSkateOffset)=350; D10=TableRollerDriveSupportAngle; E10(TableRollerDriveSupportAngle)=13.5; A11=RearSkateOffset; B11(RearSkateOffset)=150; D11=TableRollerSideAngle; E11(TableRollerSideAngle)=20; A13=CablePulleyDiameter; B13(CablePulleyDiameter)=120; D13=RoomWidth; E13(RoomWidth)=3650; D14=RoomLength; E14(RoomLength)=3650; A15=ExtensionDriverOffsetX; B15(ExtensionDriverOffsetX)=100; D15=RoomHeight; E15(RoomHeight)=2440; A16=ExtensionDriverOffsetY; B16(ExtensionDriverOffsetY)=-36
---- part PlayStation5.FCStd = doc fcstd_acdc08b8ce65 ----
FCSTD DOCUMENT  (FreeCAD 0.20R29177 +426 (Git))
Label: PlayStation5
License: All rights reserved
LicenseURL: http://en.wikipedia.org/wiki/All_rights_reserved
objects: App::DocumentObjectGroup×3, PartDesign::CoordinateSystem×1, App::FeaturePython×1, Sketcher::SketchObject×1, PartDesign::Pad×1, PartDesign::Body×1, App::Part×1
note: 5 computed .brp shape members not serialized (recipe doc carries the construction recipe); baked Part::Feature solids carry a one-line shape summary decoded from their .brp

FEATURE [App::DocumentObjectGroup] Parts
FEATURE [PartDesign::CoordinateSystem] LCS_Origin
  AttacherType = Attacher::AttachEngine3D
  MapMode = 2
  Support = -> [X_Axis]
FEATURE [App::FeaturePython] Variables  # WARN: FeaturePython — macro-defined, semantics opaque (R4)
  Type = App::PropertyContainer
FEATURE [App::DocumentObjectGroup] Constraints
FEATURE [App::DocumentObjectGroup] Configurations
FEATURE [Sketcher::SketchObject] Sketch
  FullyConstrained = true
  MapMode = 5
  Support = -> [XY_Plane001]
  sketch-geometry (10):
    g0: ArcOfCircle CenterX=-121.54 CenterY=187.58 CenterZ=0 NormalX=0 NormalY=0 NormalZ=1 AngleXU=0 Radius=8 StartAngle=1.5708 EndAngle=3.14159
    g1: LineSegment StartX=-121.54 StartY=195.58 StartZ=0 EndX=121.54 EndY=195.58 EndZ=0
    g2: ArcOfCircle CenterX=121.54 CenterY=187.58 CenterZ=0 NormalX=0 NormalY=0 NormalZ=1 AngleXU=0 Radius=8 StartAngle=-9e-16 EndAngle=1.5708
    g3: LineSegment StartX=129.54 StartY=187.58 StartZ=0 EndX=129.54 EndY=-187.58 EndZ=0
    g4: ArcOfCircle CenterX=121.54 CenterY=-187.58 CenterZ=0 NormalX=0 NormalY=0 NormalZ=1 AngleXU=0 Radius=8 StartAngle=4.71239 EndAngle=6.28319
    g5: LineSegment StartX=121.54 StartY=-195.58 StartZ=0 EndX=-121.54 EndY=-195.58 EndZ=0
    g6: ArcOfCircle CenterX=-121.54 CenterY=-187.58 CenterZ=0 NormalX=0 NormalY=0 NormalZ=1 AngleXU=0 Radius=8 StartAngle=3.14159 EndAngle=4.71239
    g7: LineSegment StartX=-129.54 StartY=-187.58 StartZ=0 EndX=-129.54 EndY=187.58 EndZ=0
    g8: GeomPoint X=-129.54 Y=195.58 Z=0
    g9: GeomPoint X=129.54 Y=-195.58 Z=0
  constraints (23):
    c: Tangent(g0,g1) = 1.5708
    c: Tangent(g1,g2) = 1.5708
    c: Tangent(g2,g3) = 1.5708
    c: Tangent(g3,g4) = 1.5708
    c: Tangent(g4,g5) = 1.5708
    c: Tangent(g5,g6) = 1.5708
    c: Tangent(g6,g7) = 1.5708
    c: Tangent(g7,g0) = 1.5708
    c: Horizontal(g1)
    c: Horizontal(g5)
    c: Vertical(g3)
    c: Vertical(g7)
    c: Equal(g0,g2)
    c: Equal(g2,g4)
    c: Equal(g4,g6)
    c: PointOnObject(g8,g1)
    c: PointOnObject(g8,g7)
    c: PointOnObject(g9,g3)
    c: PointOnObject(g9,g5)
    c: Symmetric(g4,g0,g-1)
    c: Radius(g2) = 8
    c: DistanceX(g6,g3) = 259.08
    c: DistanceY(g4,g1) = 391.16
FEATURE [PartDesign::Pad] Pad
  Direction = (0,0,1)
  Length = 91.44
  Length2 = 10
  Profile = -> Sketch
  ReferenceAxis = -> Sketch [N_Axis]
  Type = 0
FEATURE [PartDesign::Body] Body
  Group = -> [Sketch,Pad]
  Origin = -> Origin001
  Tip = -> Pad
FEATURE [App::Part] Assembly
  AssemblyType = Part::Link
  Group = -> [LCS_Origin,Variables,Constraints,Configurations,Body]
  Origin = -> Origin
  Type = Assembly
